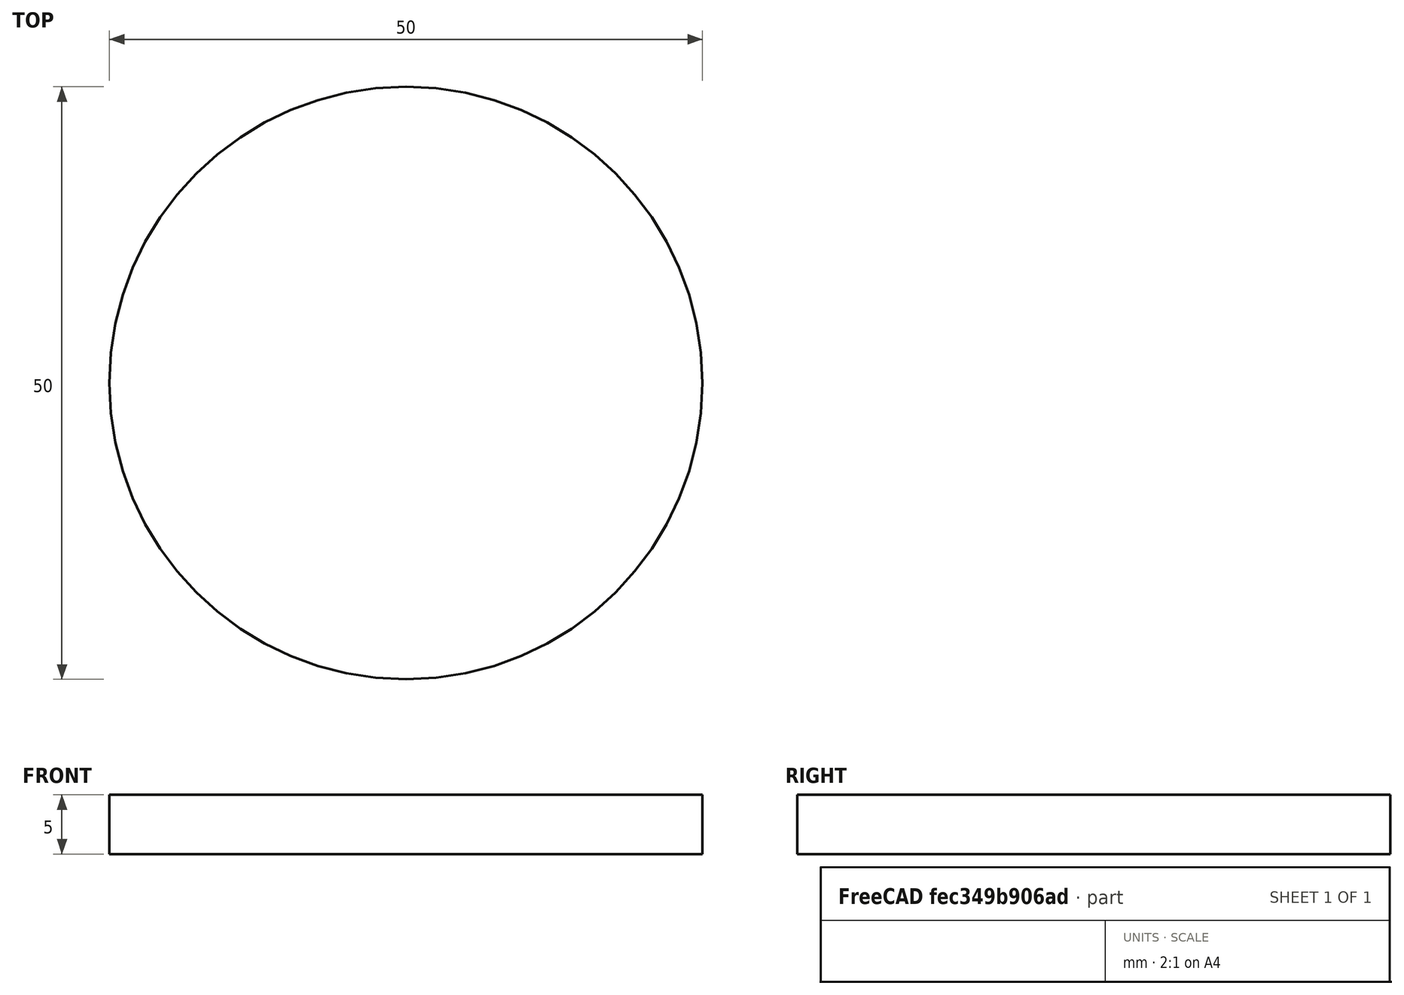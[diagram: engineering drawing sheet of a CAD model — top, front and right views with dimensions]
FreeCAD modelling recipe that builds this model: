
FCSTD DOCUMENT  (FreeCAD 0.17R13509 (Git))
Label: FTinsulator_backplate
License: All rights reserved
LicenseURL: http://en.wikipedia.org/wiki/All_rights_reserved
objects: Path::FeaturePython×6, Part::Cylinder×5, Part::MultiFuse×2, Part::Cut×2, Part::FeaturePython×2, Part::Box×1, App::FeaturePython×1, Path::FeatureCompoundPython×1
note: 15 computed .brp shape members not serialized (recipe doc carries the construction recipe); baked Part::Feature solids carry a one-line shape summary decoded from their .brp

FEATURE [Part::Cylinder] Cylinder096  label="Feedthrough009"
  Angle = 360
  AttacherType = Attacher::AttachEngine3D
  Height = 5
  Placement = pos=(73.66,148,-10) rot=(0,0,1;0rad)
  Radius = 17
  expr: Radius = 17
  expr: Placement.Base.x = 210.81999999999999 / 2 - 31.75
FEATURE [Part::Box] Box017  label="FTInsLug001"
  AttacherType = Attacher::AttachEngine3D
  Height = 5
  Length = 45.5
  Placement = pos=(51,144,-10) rot=(0,0,1;0rad)
  Width = 8
FEATURE [Part::Cylinder] Cylinder097  label="FTInsInnerHole002"
  Angle = 360
  AttacherType = Attacher::AttachEngine3D
  Height = 33
  Placement = pos=(73.66,148,-10) rot=(0,0,1;0rad)
  Radius = 12
  expr: Placement.Base.x = 210.81999999999999 / 2 - 31.75
FEATURE [Part::Cylinder] Cylinder098  label="FTInsMount003"
  Angle = 360
  AttacherType = Attacher::AttachEngine3D
  Height = 14
  Placement = pos=(53.66,148,-15) rot=(0,0,1;0rad)
  Radius = 1.7
  expr: Placement.Base.x = 73.659999999999997 - 20
FEATURE [Part::Cylinder] Cylinder099  label="FTInsMount004"
  Angle = 360
  AttacherType = Attacher::AttachEngine3D
  Height = 14
  Placement = pos=(93.66,148,-14) rot=(0,0,1;0rad)
  Radius = 1.7
  expr: Placement.Base.x = 73.659999999999997 + 20
FEATURE [Part::MultiFuse] Fusion041
  Shapes = -> [Cylinder099,Cylinder098,Cylinder097]
FEATURE [Part::MultiFuse] Fusion042
  Shapes = -> [Cylinder096,Box017]
FEATURE [Part::Cut] Cut011  label="FTInsBackplate"
  Base = -> Fusion042
  Placement = pos=(-73.66,-148,2) rot=(0,0,1;0rad)
  Tool = -> Fusion041
FEATURE [Part::Cylinder] Cylinder
  Angle = 360
  AttacherType = Attacher::AttachEngine3D
  Height = 10
  Placement = pos=(0,57,0) rot=(0,0,1;0rad)
  Radius = 2
FEATURE [Part::Cut] Cut
  Base = -> Cut011
  Placement = pos=(0,0,0) rot=(0,0,1;1.5708rad)
  Tool = -> Cylinder
FEATURE [App::FeaturePython] SetupSheet  # Path/CAM operation (typed FeaturePython)
  ClearanceHeightExpression = StartDepth+SetupSheet.ClearanceHeightOffset
  ClearanceHeightOffset = 5
  FinalDepthExpression = OpFinalDepth
  HorizRapid = 0
  SafeHeightExpression = StartDepth+SetupSheet.SafeHeightOffset
  SafeHeightOffset = 3
  StartDepthExpression = OpStartDepth
  StepDownExpression = OpToolDiameter
  VertRapid = 0
FEATURE [Part::FeaturePython] Clone  label="Base-Cut"  # Draft clone (typed FeaturePython)
  AttacherType = Attacher::AttachEngine3D
  Fuse = false
  Objects = -> [Cut]
  PathResource = Base
  Placement = pos=(0,0,0) rot=(0,0,1;1.5708rad)
  Scale = (1,1,1)
FEATURE [Part::FeaturePython] Stock001  # WARN: FeaturePython — macro-defined, semantics opaque (R4)
  Height = 5
  Placement = pos=(0,0.09,-8) rot=(0,0,1;0rad)
  Radius = 25
  StockType = CreateCylinder
FEATURE [Path::FeaturePython] T1__125_End_Mill  label="T1: 125 End Mill"  # Path/CAM operation (typed FeaturePython)
  HorizFeed = 1500
  HorizRapid = 0
  SpindleDir = 0
  SpindleSpeed = 24000
  ToolNumber = 1
  VertFeed = 40
  VertRapid = 0
  expr: HorizRapid = SetupSheet.HorizRapid
  expr: VertRapid = SetupSheet.VertRapid
FEATURE [Path::FeaturePython] Contour  # Path/CAM operation (typed FeaturePython)
  Active = true
  AreaParams:
    OpenMode = 0
    Angle = 45.0
    MinArcPoints = 4
    Coplanar = 2
    Tolerance = 1e-07
    CleanDistance = 0.0
    PocketExtraOffset = 0.0
    RoundPrecision = 0.0
    AngleShift = 0.0
    SubjectFill = 0
    PocketMode = 0
    Simplify = False
    SectionTolerance = 1e-06
    MaxArcPoints = 100
    Offset = 1.585
    Accuracy = 0.01
    PocketStepover = 0.0
    ClipFill = 0
    ToolRadius = 1.0
    Outline = False
    ClipperScale = 10000000.0
    FromCenter = False
    Explode = False
    EndType = 0
    Shift = 0.0
    ExtraPass = 0
    Project = False
    JoinType = 0
    Thicken = False
    Stepdown = 1.0
    SectionMode = 2
    MiterLimit = 2.0
    Deflection = 0.01
    Reorient = True
    FitArcs = True
    SectionCount = -1
    SectionOffset = 0.0
    Stepover = 0.0
    Unit = 1.0
    Fill = 0
  ClearanceHeight = 5
  Direction = 0
  FinalDepth = -9
  JoinType = 0
  MiterLimit = 0.1
  OffsetExtra = 0
  OpFinalDepth = -8
  OpStartDepth = -3
  OpToolDiameter = 3.17
  PathParams = {'resume_height': 3.0, 'feedrate': 1500.0, 'verbose': True, 'orientation': 1, 'return_end': True, 'preamble': False, 'retraction': 5.0, 'feedrate_v': 40.0}
  SafeHeight = 3
  Side = 0
  StartDepth = 0
  StartPoint = (0,0,0)
  StepDown = 1.5
  ToolController = -> T1__125_End_Mill
  UseComp = true
  UseStartPoint = false
  expr: ClearanceHeight = StartDepth + SetupSheet.ClearanceHeightOffset
  expr: SafeHeight = StartDepth + SetupSheet.SafeHeightOffset
  expr: StepDown = 1.5
  expr: FinalDepth = -9
  expr: StartDepth = 0
FEATURE [Path::FeaturePython] Profile_Faces  # Path/CAM operation (typed FeaturePython)
  Active = true
  AreaParams:
    OpenMode = 0
    Angle = 45.0
    MinArcPoints = 4
    Coplanar = 0
    Tolerance = 1e-07
    CleanDistance = 0.0
    PocketExtraOffset = 0.0
    RoundPrecision = 0.0
    AngleShift = 0.0
    SubjectFill = 0
    PocketMode = 0
    Simplify = False
    SectionTolerance = 1e-06
    MaxArcPoints = 100
    Offset = -1.585
    Accuracy = 0.01
    PocketStepover = 0.0
    ClipFill = 0
    ToolRadius = 1.0
    Outline = False
    ClipperScale = 10000000.0
    FromCenter = False
    Explode = False
    EndType = 0
    Shift = 0.0
    ExtraPass = 0
    Project = False
    JoinType = 0
    Thicken = False
    Stepdown = 1.0
    SectionMode = 2
    MiterLimit = 2.0
    Deflection = 0.01
    Reorient = True
    FitArcs = True
    SectionCount = -1
    SectionOffset = 0.0
    Stepover = 0.0
    Unit = 1.0
    Fill = 0
  Base = -> [Clone]
  ClearanceHeight = 2
  Direction = 0
  FinalDepth = -9
  JoinType = 0
  MiterLimit = 0.1
  OffsetExtra = 0
  OpFinalDepth = -8
  OpStartDepth = -3
  OpToolDiameter = 3.17
  PathParams = {'resume_height': 0.0, 'feedrate': 1500.0, 'verbose': True, 'orientation': 1, 'return_end': True, 'preamble': False, 'retraction': 2.0, 'feedrate_v': 40.0}
  SafeHeight = 0
  Side = 1
  StartDepth = -3
  StartPoint = (0,0,0)
  StepDown = 1.5
  ToolController = -> T1__125_End_Mill
  UseComp = true
  UseStartPoint = false
  processCircles = false
  processHoles = false
  processPerimeter = true
  expr: ClearanceHeight = StartDepth + SetupSheet.ClearanceHeightOffset
  expr: SafeHeight = StartDepth + SetupSheet.SafeHeightOffset
  expr: StepDown = 1.5
  expr: FinalDepth = -9
  expr: StartDepth = -3
FEATURE [Path::FeaturePython] MillFace  # Path/CAM operation (typed FeaturePython)
  Active = true
  AreaParams:
    OpenMode = 0
    Angle = 45.0
    MinArcPoints = 4
    Coplanar = 0
    Tolerance = 1e-07
    CleanDistance = 0.0
    PocketExtraOffset = -1.5
    RoundPrecision = 0.0
    AngleShift = 0.0
    SubjectFill = 0
    PocketMode = 1
    Simplify = False
    SectionTolerance = 1e-06
    MaxArcPoints = 100
    Offset = 0.0
    Accuracy = 0.01
    PocketStepover = 1.585
    ClipFill = 0
    ToolRadius = 1.585
    Outline = False
    ClipperScale = 10000000.0
    FromCenter = True
    Explode = False
    EndType = 0
    Shift = 0.0
    ExtraPass = 0
    Project = False
    JoinType = 0
    Thicken = False
    Stepdown = 1.0
    SectionMode = 2
    MiterLimit = 2.0
    Deflection = 0.01
    Reorient = True
    FitArcs = True
    SectionCount = -1
    SectionOffset = 0.0
    Stepover = 0.0
    Unit = 1.0
    Fill = 0
  BoundaryShape = 0
  ClearanceHeight = 5
  CutMode = 0
  ExtraOffset = 1.5
  FinalDepth = -3
  FinishDepth = 0
  KeepToolDown = false
  MinTravel = false
  OffsetPattern = 0
  OpFinalDepth = -3
  OpStartDepth = -1.5
  OpToolDiameter = 3.17
  PathParams = {'resume_height': 3.0, 'feedrate': 1500.0, 'verbose': True, 'orientation': 1, 'return_end': True, 'preamble': False, 'retraction': 5.0, 'feedrate_v': 40.0}
  SafeHeight = 3
  StartAt = 0
  StartDepth = 0
  StartPoint = (0,0,0)
  StepDown = 1.5
  StepOver = 50
  ToolController = -> T1__125_End_Mill
  UseStartPoint = false
  ZigZagAngle = 45
  expr: ClearanceHeight = StartDepth + SetupSheet.ClearanceHeightOffset
  expr: SafeHeight = StartDepth + SetupSheet.SafeHeightOffset
  expr: StepDown = 1.5
  expr: FinalDepth = OpFinalDepth
  expr: StartDepth = 0
FEATURE [Path::FeaturePython] Drilling  # Path/CAM operation (typed FeaturePython)
  Active = true
  AddTipLength = false
  Base = -> [Clone]
  ClearanceHeight = 2
  DwellEnabled = false
  DwellTime = 0
  FinalDepth = -8
  OpFinalDepth = -8
  OpStartDepth = -3
  OpToolDiameter = 3.17
  PeckDepth = 0
  PeckEnabled = false
  RetractHeight = 10
  ReturnLevel = 0
  SafeHeight = 0
  StartDepth = -3
  ToolController = -> T1__125_End_Mill
  expr: ClearanceHeight = StartDepth + SetupSheet.ClearanceHeightOffset
  expr: SafeHeight = StartDepth + SetupSheet.SafeHeightOffset
  expr: FinalDepth = OpFinalDepth
  expr: StartDepth = OpStartDepth
FEATURE [Path::FeatureCompoundPython] Operations  # Path/CAM operation (typed FeaturePython)
  Group = -> [MillFace,Profile_Faces,Drilling,Contour]
  UsePlacements = false
FEATURE [Path::FeaturePython] Job  # Path/CAM operation (typed FeaturePython)
  Base = -> Clone
  GeometryTolerance = 0.01
  Operations = -> Operations
  PostProcessor = 5
  PostProcessorOutputFile = <userpath>/Documents/CNC/chamber_plate/fts/ftinsulator1_backplate_125_roughing_new.ngc
  SetupSheet = -> SetupSheet
  Stock = -> Stock001
  ToolController = -> [T1__125_End_Mill]
